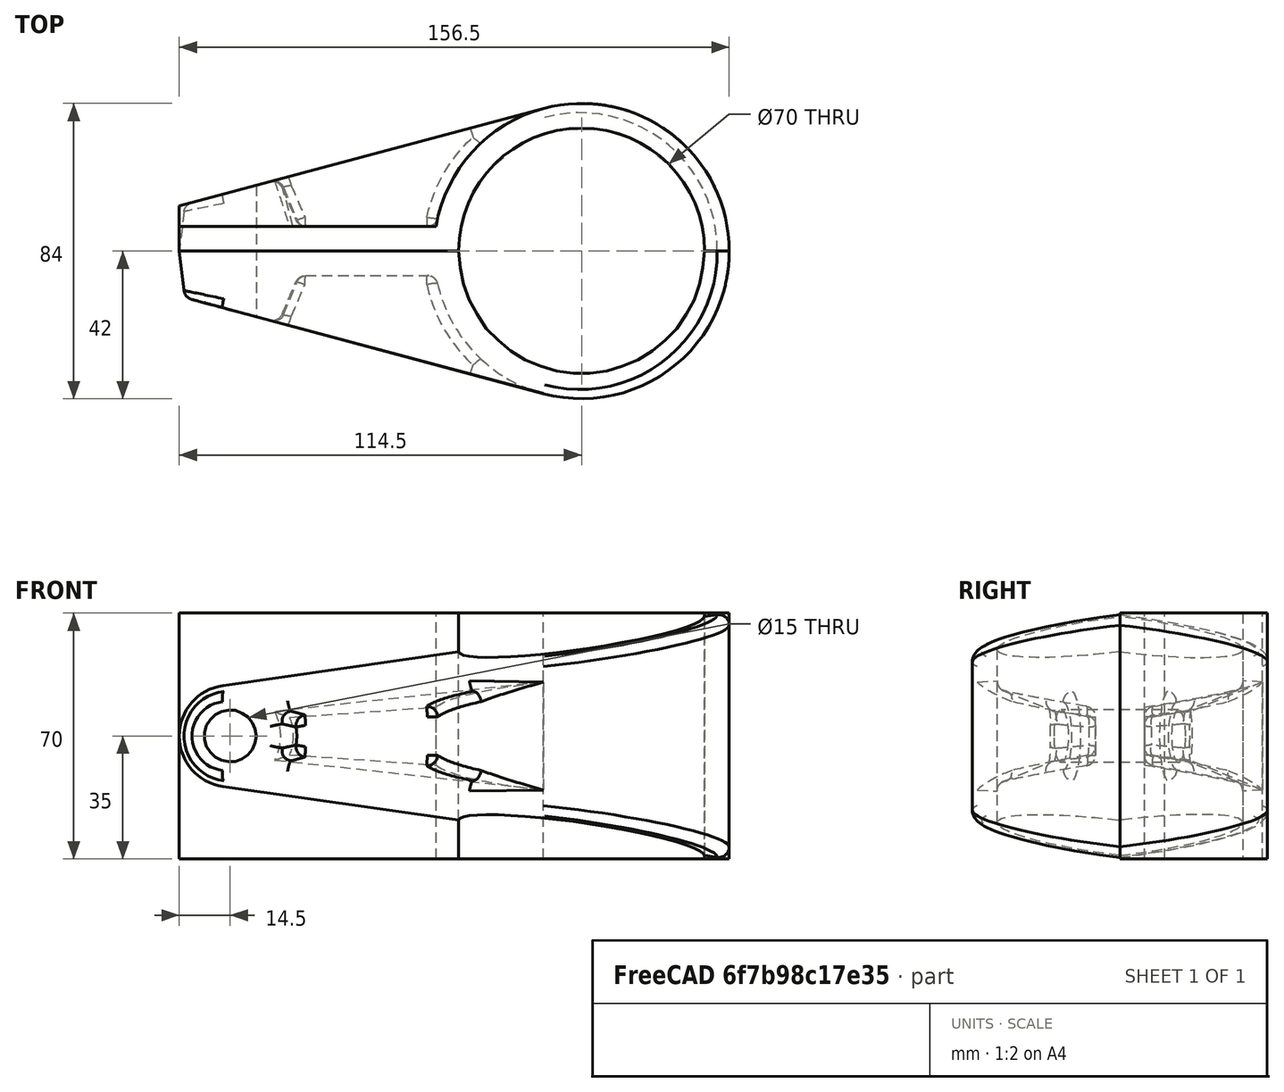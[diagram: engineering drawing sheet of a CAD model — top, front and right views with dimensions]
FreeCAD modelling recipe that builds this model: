
FCSTD DOCUMENT  (FreeCAD 1.0R39319 (Git))
Label: Mania2002
License: All rights reserved
LicenseURL: https://en.wikipedia.org/wiki/All_rights_reserved
objects: Sketcher::SketchObject×6, PartDesign::Pad×4, PartDesign::Body×4, PartDesign::Boolean×3, PartDesign::Draft×3, PartDesign::SubShapeBinder×2, Spreadsheet::Sheet×1, PartDesign::Pocket×1, PartDesign::Fillet×1, PartDesign::Mirrored×1
note: 53 computed .brp shape members not serialized (recipe doc carries the construction recipe); baked Part::Feature solids carry a one-line shape summary decoded from their .brp

FEATURE [Spreadsheet::Sheet] Spreadsheet
  cells = A1='MainDiameter; B1(LargeDiameter)=70; A2='SubDiameter; B2(SmallDiameter)=15; A3='Length; B3(Distance)=100; A4='Thickness; B4(Thickness)=7; A5='Angle; B5=7; A6='Ramp; B6=15; A7='Fillet; B7(Fillet)=3
FEATURE [Sketcher::SketchObject] Sketch  label="Main outline"
  ArcFitTolerance = 1e-06
  AttachmentSupport = -> [XY_Plane]
  FullyConstrained = true
  MakeInternals = false
  MapMode = 5
  expr: Constraints[0] = Spreadsheet.B6
  expr: Constraints[11] = Spreadsheet.B3
  expr: Constraints[12] = Spreadsheet.B2 / 2 + Spreadsheet.B4
  expr: Constraints[14] = Spreadsheet.LargeDiameter / 2
  expr: Constraints[17] = Spreadsheet.Thickness
  sketch-geometry (7):
    g0: ArcOfCircle CenterX=0 CenterY=0 CenterZ=0 NormalX=0 NormalY=0 NormalZ=1 AngleXU=0 Radius=42 StartAngle=0 EndAngle=1.8326
    g1: LineSegment StartX=-10.8704 StartY=40.5689 StartZ=0 EndX=-114.5 EndY=12.8014 EndZ=0
    g2: LineSegment StartX=-114.5 StartY=12.8014 StartZ=0 EndX=-114.5 EndY=0 EndZ=0
    g3: LineSegment StartX=-114.5 StartY=0 StartZ=0 EndX=-100 EndY=0 EndZ=0
    g4: LineSegment StartX=-100 StartY=0 StartZ=0 EndX=-35 EndY=4.3e-15 EndZ=0
    g5: LineSegment StartX=35 StartY=0 StartZ=0 EndX=42 EndY=0 EndZ=0
    g6: ArcOfCircle CenterX=0 CenterY=0 CenterZ=0 NormalX=0 NormalY=0 NormalZ=1 AngleXU=0 Radius=35 StartAngle=0 EndAngle=3.14159
  constraints (20):
    c: Angle(g-1,g1) = 0.261799
    c: Tangent(g0,g1) = -1.5708
    c: Coincident(g0,g-1)
    c: Coincident(g2,g1)
    c: Vertical(g2)
    c: PointOnObject(g2,g-1)
    c: PointOnObject(g0,g-1)
    c: Coincident(g2,g3)
    c: PointOnObject(g3,g-1)
    c: Coincident(g3,g4)
    c: Coincident(g5,g0)
    c: DistanceX(g3,g-1) = 100
    c: DistanceX(g3,g3) = 14.5
    c: Coincident(g6,g0)
    c: Radius(g6) = 35
    c: Coincident(g5,g6)
    c: PointOnObject(g5,g-1)
    c: Distance(g5,g5) = 7
    c: Coincident(g4,g6)
    c: PointOnObject(g4,g-1)
FEATURE [Sketcher::SketchObject] Sketch001  label="base"
  ArcFitTolerance = 1e-06
  AttachmentSupport = -> [XY_Plane]
  FullyConstrained = true
  MakeInternals = false
  MapMode = 5
  expr: Constraints[0] = Spreadsheet.B6
  expr: Constraints[11] = Spreadsheet.B3
  expr: Constraints[12] = Spreadsheet.B2 / 2 + Spreadsheet.B4
  expr: Constraints[14] = Spreadsheet.LargeDiameter / 2
  expr: Constraints[17] = Spreadsheet.Thickness
  sketch-geometry (7):
    g0: ArcOfCircle CenterX=0 CenterY=0 CenterZ=0 NormalX=0 NormalY=0 NormalZ=1 AngleXU=0 Radius=42 StartAngle=0 EndAngle=1.8326
    g1: LineSegment StartX=-10.8704 StartY=40.5689 StartZ=0 EndX=-114.5 EndY=12.8014 EndZ=0
    g2: LineSegment StartX=-114.5 StartY=12.8014 StartZ=0 EndX=-114.5 EndY=0 EndZ=0
    g3: LineSegment StartX=-114.5 StartY=0 StartZ=0 EndX=-100 EndY=0 EndZ=0
    g4: LineSegment StartX=-100 StartY=0 StartZ=0 EndX=-35 EndY=4.3e-15 EndZ=0
    g5: LineSegment StartX=35 StartY=0 StartZ=0 EndX=42 EndY=0 EndZ=0
    g6: ArcOfCircle CenterX=0 CenterY=0 CenterZ=0 NormalX=0 NormalY=0 NormalZ=1 AngleXU=0 Radius=35 StartAngle=0 EndAngle=3.14159
  constraints (20):
    c: Angle(g-1,g1) = 0.261799
    c: Tangent(g0,g1) = -1.5708
    c: Coincident(g0,g-1)
    c: Coincident(g2,g1)
    c: Vertical(g2)
    c: PointOnObject(g2,g-1)
    c: PointOnObject(g0,g-1)
    c: Coincident(g2,g3)
    c: PointOnObject(g3,g-1)
    c: Coincident(g3,g4)
    c: Coincident(g5,g0)
    c: DistanceX(g3,g-1) = 100
    c: DistanceX(g3,g3) = 14.5
    c: Coincident(g6,g0)
    c: Radius(g6) = 35
    c: Coincident(g5,g6)
    c: PointOnObject(g5,g-1)
    c: Distance(g5,g5) = 7
    c: Coincident(g4,g6)
    c: PointOnObject(g4,g-1)
FEATURE [PartDesign::Pad] Pad
  Direction = (0,0,1)
  Length = 70
  Length2 = 10
  Midplane = true
  Profile = -> Sketch001
  ReferenceAxis = -> Sketch001 [N_Axis]
  Refine = true
  Suppressed = false
  Type = 0
FEATURE [PartDesign::Body] Body
  AllowCompound = false
  Group = -> [Sketch,Sketch001,Pad]
  Origin = -> Origin
  Tip = -> Pad
FEATURE [Sketcher::SketchObject] Sketch003
  ArcFitTolerance = 1e-06
  AttachmentSupport = -> [XZ_Plane001]
  FullyConstrained = true
  MakeInternals = false
  MapMode = 5
  Placement = pos=(0,0,0) rot=(1,0,0;1.5708rad)
  expr: Constraints[5] = Spreadsheet.Distance
  sketch-geometry (4):
    g0: LineSegment StartX=42 StartY=35 StartZ=0 EndX=42 EndY=-35 EndZ=0
    g1: LineSegment StartX=42 StartY=-35 StartZ=0 EndX=-102.057 EndY=-14.3533 EndZ=0
    g2: ArcOfCircle CenterX=-100 CenterY=0 CenterZ=0 NormalX=0 NormalY=0 NormalZ=1 AngleXU=0 Radius=14.5 StartAngle=1.71315 EndAngle=4.57004
    g3: LineSegment StartX=-102.057 StartY=14.3533 StartZ=0 EndX=42 EndY=35 EndZ=0
  constraints (9):
    c: Coincident(g-3,g0)
    c: Coincident(g0,g-3)
    c: Coincident(g0,g1)
    c: Coincident(g3,g0)
    c: Tangent(g2,g-4)
    c: DistanceX(g2,g-1) = 100
    c: Tangent(g2,g3) = 1.5708
    c: Tangent(g1,g2) = 1.5708
    c: PointOnObject(g2,g-1)
FEATURE [PartDesign::Pad] Pad002
  Direction = (0,-1,2e-16)
  Length = 50
  Length2 = 10
  Placement = pos=(0,0,0) rot=(1,0,0;1.5708rad)
  Profile = -> Sketch003
  ReferenceAxis = -> Sketch003 [N_Axis]
  Refine = true
  Reversed = true
  Suppressed = false
  Type = 0
FEATURE [PartDesign::Boolean] Boolean
  BaseFeature = -> Pad002
  Group = -> [Body]
  Refine = true
  Suppressed = false
  Type = 2
  UsePlacement = true
FEATURE [PartDesign::Draft] Draft
  Angle = 7
  Base = -> Boolean [Face8,Face2,Face4]
  BaseFeature = -> Boolean
  NeutralPlane = -> Boolean [Face6]
  Refine = true
  SupportTransform = false
  Suppressed = false
FEATURE [Sketcher::SketchObject] Sketch004
  ArcFitTolerance = 1e-06
  AttachmentSupport = -> [Draft]
  ExternalGeometry = -> [Draft]
  FullyConstrained = true
  MakeInternals = false
  MapMode = 5
  Placement = pos=(0,0,0) rot=(1,0,0;1.5708rad)
  expr: Constraints[1] = Spreadsheet.SmallDiameter
  sketch-geometry (1):
    g0: Circle CenterX=-100 CenterY=0 CenterZ=0 NormalX=0 NormalY=0 NormalZ=1 AngleXU=0 Radius=7.5
  constraints (2):
    c: Coincident(g0,g-3)
    c: Diameter(g0) = 15
FEATURE [PartDesign::Pocket] Pocket
  BaseFeature = -> Draft
  Direction = (0,1,-2e-16)
  Length = 5
  Length2 = 5
  Profile = -> Sketch004
  ReferenceAxis = -> Sketch004 [N_Axis]
  Refine = true
  Suppressed = false
  Type = 1
FEATURE [PartDesign::SubShapeBinder] Binder
  BindCopyOnChange = 0
  BindMode = 0
  ClaimChildren = false
  Context = -> Body001 [Boolean002.Body003.Boolean001.Body002.Binder.]
  Fuse = false
  MakeFace = true
  OffsetFill = false
  OffsetIntersection = false
  OffsetJoinType = 0
  OffsetOpenResult = false
  PartialLoad = false
  Refine = true
  Relative = true
  Support = -> [Body001[Boolean.Body.Sketch001.]]
  _Version = 2
FEATURE [Sketcher::SketchObject] Sketch005
  ArcFitTolerance = 1e-06
  AttachmentSupport = -> [XY_Plane002]
  ExternalGeometry = -> [Binder]
  FullyConstrained = true
  MakeInternals = false
  MapMode = 5
  sketch-geometry (4):
    g0: LineSegment StartX=-114.5 StartY=7 StartZ=0 EndX=-41.4126 EndY=7 EndZ=0
    g1: LineSegment StartX=-10.8704 StartY=40.5689 StartZ=0 EndX=-114.5 EndY=12.8014 EndZ=0
    g2: LineSegment StartX=-114.5 StartY=12.8014 StartZ=0 EndX=-114.5 EndY=7 EndZ=0
    g3: ArcOfCircle CenterX=0 CenterY=0 CenterZ=0 NormalX=0 NormalY=0 NormalZ=1 AngleXU=0 Radius=42 StartAngle=1.8326 EndAngle=2.97414
  constraints (10):
    c: PointOnObject(g0,g-5)
    c: Horizontal(g0)
    c: Coincident(g1,g2)
    c: Coincident(g2,g0)
    c: Distance(g-1,g0) = 7
    c: Coincident(g1,g-5)
    c: Coincident(g3,g-1)
    c: Coincident(g3,g1)
    c: Coincident(g3,g0)
    c: Coincident(g1,g-4)
FEATURE [PartDesign::Pad] Pad003
  Direction = (0,0,1)
  Length = 70
  Length2 = 10
  Midplane = true
  Profile = -> Sketch005
  ReferenceAxis = -> Sketch005 [N_Axis]
  Refine = true
  Suppressed = false
  Type = 0
FEATURE [PartDesign::Body] Body002
  AllowCompound = false
  Group = -> [Binder,Sketch005,Pad003]
  Origin = -> Origin002
  Tip = -> Pad003
FEATURE [PartDesign::SubShapeBinder] Binder001
  BindCopyOnChange = 0
  BindMode = 0
  ClaimChildren = false
  Context = -> Body001 [Boolean002.Body003.Binder001.]
  Fuse = false
  MakeFace = true
  OffsetFill = false
  OffsetIntersection = false
  OffsetJoinType = 0
  OffsetOpenResult = false
  PartialLoad = false
  Refine = true
  Relative = true
  Support = -> [Body001[Pocket.Face7]]
  _Version = 2
FEATURE [Sketcher::SketchObject] Sketch006
  ArcFitTolerance = 1e-06
  AttachmentSupport = -> [Binder001]
  ExternalGeometry = -> [Binder001]
  FullyConstrained = true
  MakeInternals = false
  MapMode = 5
  Placement = pos=(-10.8704,40.5689,0) rot=(-0.092692,0.704063,0.704063;3.32645rad)
  expr: Constraints[14] = Spreadsheet.Thickness
  expr: Constraints[15] = Spreadsheet.Thickness
  expr: Constraints[3] = Spreadsheet.Thickness
  sketch-geometry (6):
    g0: LineSegment StartX=-3.6e-15 StartY=-15.3509 StartZ=0 EndX=79.2342 EndY=-6.92547 EndZ=0
    g1: LineSegment StartX=-3.6e-15 StartY=15.3509 StartZ=0 EndX=79.2342 EndY=6.92547 EndZ=0
    g2: LineSegment StartX=-3.6e-15 StartY=15.3509 StartZ=0 EndX=-3.6e-15 EndY=-15.3509 EndZ=0
    g3: ArcOfCircle CenterX=92.2738 CenterY=-3.7e-15 CenterZ=0 NormalX=0 NormalY=0 NormalZ=1 AngleXU=0 Radius=14.7646 StartAngle=2.65337 EndAngle=3.62982
    g4: GeomPoint X=77.5092 Y=0 Z=0
    g5: GeomPoint X=84.5092 Y=0 Z=0
  constraints (16):
    c: Parallel(g0,g-5)
    c: Coincident(g2,g1)
    c: Coincident(g2,g0)
    c: Distance(g0,g-5) = 7
    c: PointOnObject(g0,g-3)
    c: Parallel(g-4,g1)
    c: Vertical(g2)
    c: Coincident(g3,g-6)
    c: Coincident(g3,g1)
    c: Coincident(g3,g0)
    c: PointOnObject(g4,g3)
    c: PointOnObject(g5,g-6)
    c: PointOnObject(g5,g-1)
    c: PointOnObject(g4,g-1)
    c: DistanceX(g4,g5) = 7
    c: Distance(g-4,g1) = 7
FEATURE [PartDesign::Pad] Pad004
  Direction = (-0.258819,0.965926,0)
  Length = 50
  Length2 = 10
  Profile = -> Sketch006
  ReferenceAxis = -> Sketch006 [N_Axis]
  Refine = true
  Reversed = true
  Suppressed = false
  Type = 0
FEATURE [PartDesign::Boolean] Boolean001
  BaseFeature = -> Pad004
  Group = -> [Body002]
  Refine = true
  Suppressed = false
  Type = 2
  UsePlacement = true
FEATURE [PartDesign::Draft] Draft001
  Angle = 7
  Base = -> Boolean001 [Face5,Face3]
  BaseFeature = -> Boolean001
  Refine = true
  SupportTransform = false
  Suppressed = false
FEATURE [PartDesign::Body] Body003
  AllowCompound = false
  Group = -> [Binder001,Sketch006,Pad004,Boolean001,Draft001]
  Origin = -> Origin003
  Tip = -> Draft001
FEATURE [PartDesign::Boolean] Boolean002
  BaseFeature = -> Pocket
  Group = -> [Body003]
  Refine = true
  Suppressed = false
  Type = 1
  UsePlacement = true
FEATURE [PartDesign::Draft] Draft002
  Angle = 7
  Base = -> Boolean002 [Face10]
  BaseFeature = -> Boolean002
  Refine = true
  SupportTransform = false
  Suppressed = false
FEATURE [PartDesign::Fillet] Fillet
  Base = -> Draft002 [Edge32,Edge23,Edge31,Edge28,Edge29,Edge33,Edge34,Edge30,Edge22,Edge24,Edge35,Edge19]
  BaseFeature = -> Draft002
  Radius = 3
  Refine = true
  SupportTransform = false
  Suppressed = false
  UseAllEdges = false
FEATURE [PartDesign::Mirrored] Mirrored
  BaseFeature = -> Fillet
  MirrorPlane = -> XZ_Plane001
  Originals = -> [Fillet]
  Refine = true
  Suppressed = false
  TransformMode = 1
FEATURE [PartDesign::Body] Body001
  AllowCompound = false
  Group = -> [Sketch003,Pad002,Boolean,Draft,Sketch004,Pocket,Boolean002,Draft002,Fillet,Mirrored]
  Origin = -> Origin001
  Tip = -> Mirrored
